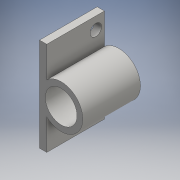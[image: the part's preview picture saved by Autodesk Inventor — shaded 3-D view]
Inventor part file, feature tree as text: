
AUTODESK INVENTOR PART (.ipt)
format: ipt  version: 2016 (Build 200138000, 138)  size: 118,272 bytes
history: native  units: mm
features: extrude x2, sketch x2
ambient origin geometry x8: Origin, YZ Plane, XZ Plane, XY Plane, X Axis, Y Axis, Z Axis, Center Point
bodies: Solid1 (feature_tree)
feature tree (4):
  extrude  "Extrusion1"  Depth=26.0mm
  extrude  "Extrusion2"  Depth=16.0mm TaperAngle=0.0deg
  sketch  "Sketch1"  dims[d0=8.8mm d2=26.0mm]
  sketch  "Sketch2"  dims[d3=2.0mm d4=16.0mm d5=0.0mm d10=3.2mm d11=3.2mm d12=16.0mm d13=0.0mm d14=2.4mm d15=2.4mm]
